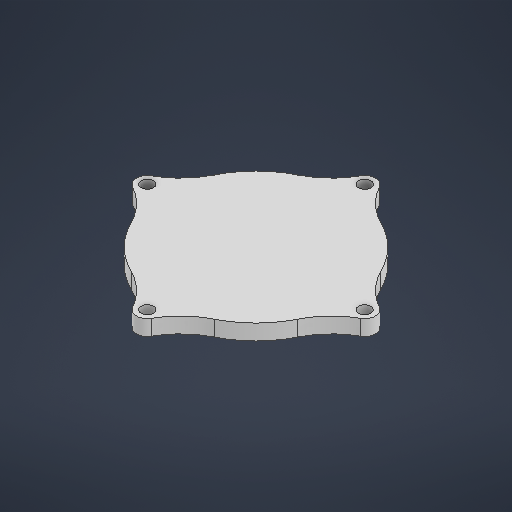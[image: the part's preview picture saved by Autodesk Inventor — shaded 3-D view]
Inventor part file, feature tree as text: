
AUTODESK INVENTOR PART (.ipt)
format: ipt  version: 2025.3 (Build 293356000, 356)  size: 210,432 bytes
history: native  units: mm
features: sketch x2, extrude x1
ambient origin geometry x8: Origin, YZ Plane, XZ Plane, XY Plane, X Axis, Y Axis, Z Axis, Center Point
bodies: Solid1 (feature_tree)
feature tree (3):
  extrude  "Extrusion1"  Depth=55.0mm
  sketch  "Sketch1"  dims[d0=60.0mm d1=55.0mm]
  sketch  "Sketch Circular Pattern1"  dims[d2=7.0mm d3=4.0mm d4=35.0mm d5=24.0mm d6=40.0mm d8=360.0deg d10=5.0mm d11=0.0mm]
